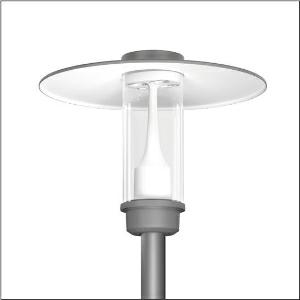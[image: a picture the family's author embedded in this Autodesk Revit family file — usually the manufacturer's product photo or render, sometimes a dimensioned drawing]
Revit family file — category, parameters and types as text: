
# Revit family: litepole_2_iq___p1_0a_5xa5425ff14h_a7e5
name_source: partatom
category: Lighting Fixtures
units: mm (PartAtom-declared; Revit-internal decimal feet)

## family parameters
Cut with Voids When Loaded = No
Host = Face
Light Source = No
Part Type = Normal
Room Calculation Point = No
Round Connector Dimension = Use Diameter
Shared = No

## types (1)
- --- (1 x LED, 1520 lm, 10.5 W, 3000K)
    Apparent Load = 11 VA
    CIE Flux Codes = 33 62 89 96 100
    Color Rendering = 70
    Color Temperature = 3000K
    Default Elevation = 1800 mm
    Description = Litepole 2 iQ, mast luminaire, Module 540 iQ-SR, primary light control with 3 zone facetted reflector, of plastic, silver coated, highly specular, structured, primary optical cover: cover, of PMMA, transparent, light distribution: P1.0a, light emission: direct distribution, primary light characteristic: strongly asymmetric, installation type: post-top, LED, High Power LED, rated luminous flux: 1.520lm, luminous efficacy: 145lm/W, light colour: 730, colour temperature: 3000K, control gear: iQ Street-Remote, control: Auto-Match, Temp-Guard, Lumen-Switch, Night-Set, Smart-Wire, Light-Fading, Desk-Remote (wireless, voltage-free reading and setting of iQ features in the workshop via application-optimized NFC function/RFID function), optimised constant luminous flux control (CLO 2.0), Street-Remote, pre-setting: logarithmic dimming characteristic, with terminal, 6-pole, max. 2.5mm², mains connection: 230..240V, AC, 50/60Hz, start of lifetime: 11W, end of service life: 11W, reduction: 5W, luminaire housing, upper part, of aluminium, coated, Siteco® metallic grey (DB 702S), diameter: 750mm, height: 590mm, spigot size: d x l = 76 x 70mm (post-top) | with reducer (optional accessory) 60 x 70mm, mounting height: 3..5m, post-top mast mounting element, of diecast aluminium, coated, Siteco® metallic grey (DB 702S), Module 540 iQ-SR, traffic white (RAL 9016), equipment: standard, protection rating (complete): IP65, insulation class (complete): insulation class II (safety insulation), certification: CE, ENEC, VDE, packaging unit: 1 piece

Light Distribution: P1.0a
    Height = 590 mm
    Lamp = 1 x LED
    Lamp Light Flux = 1520 lm
    Lamp Power = 10.5 W
    Lamp count = 1
    Length = 750 mm
    Luminous efficacy = 145 lm/W
    Manufacturer = Siteco
    ModVariant = No
    Model = 5XA5425FF14H
    Number of Poles = 1
    OnlyDefault = Yes
    Power Factor = 1
    Product Name = Litepole 2 iQ | P1.0a
    Product group = mast luminaire | pylon top
    ProductGroupID = 6100
    Protection Class = Protection class II
    Protection Degree = IP 65
    RLX_Detail_Level = 1
    RLX_Emergency_Light_Flux = 0 lm
    RLX_Emergency_Type = 0
    RLX_Emergency_Type_DB = No
    RlxData = <blob elided: 55309 chars, md5=73a9b2b2>
    Socket = socket
    Standby Power = 0 W
    System Light Flux = 1520 lm
    System Power = 11 W
    Type Comments = factory setting: luminous flux: 100 % | dim-lin: 254 | 419 mA
    Type Image = l_1006518.jpg
    URL = http://relux.com
    VarID = @adj_193759
    Voltage = 0 V
    Weight = 0.00 kg
    Width = 0 mm  [stored 0 ft]

note: [stored X ft] marks values corroborated as IEEE doubles in the binary element streams (Revit-internal decimal feet)

## geometry (parser evidence)
native form markers: Blend x4, Sweep x10
no freeform markers — native parametric forms only
